# Revit family: PRD_AR_TltRllHldrs_JumboRollHolder_CHRX669,CHRX670
name_source: partatom
category: Specialty Equipment
revit_build: Autodesk Revit 2018 (Build: 20190510_1515(x64)
units: mm (PartAtom-declared; Revit-internal decimal feet)

## family parameters
Cut with Voids When Loaded = No
Host = Face
OmniClass Number = 23.40.20.21.21
OmniClass Title = Toilet Paper Dispensers
Part Type = Normal
Room Calculation Point = No
Round Connector Dimension = Use Diameter
Shared = No

## types (2) — shared parameters
AssetType = Fixed
Category = Pr_40_20_76_88, Toilet roll holders
Color = Stainless steel
Default Elevation = 700 mm  [stored 2.29659 ft]
DurationUnit = year
FillingQuantity = 1 ROLL
Finish = Satin finished
FinishAndColour = Stainless steel, satin finished
Form = Wall mounted
IfcExportAs = IfcFurnitureType
IfcExportType = NOTDEFINED
IntegralAccessories = Stainless steel screws and dowels incl.
MainColor = Stainless steel
Manufacturer = KWC Group AG
ManufacturerName = KWC Group AG
ManufacturerURL = www.kwc.com
Material = Stainless steel
Materials = Stainless steel
NBSDescription = Toilet roll holders
NBSReference = 45-35-72/368
ProductInformation = https://pim.kwc.com
RollHolderMaterial = PRD_AR_StainlessSteel_SatinFinished
Style = Toilet roll holder
URL = www.kwc.com
Uniclass2015Code = Pr_40_20_76_88
Uniclass2015Title = Toilet roll holders
Uniclass2015Version = Products v1.5
Version = 1
WarrantyDurationUnit = year

## per-type parameters (varying)
| type | BIMObjectName | Description | Features | GrossWeight | Lock | MaximumWidthOfConsumable | ModelNumber | Name | NetWeight | NominalDepth | NominalHeight | NominalLength | NominalWidth | Size |
| CHRX670 | PRD_AR_ToiletRollHolders_JumboRollHolder_CHRX670 | Jumbo roll holder for wall mounting, stainless steel, surface satin finished, material thickness 0.9 mm, closed round casing with inspection window, paper withdrawal over two tear-off edges, locked with hexagonal allen screw, for 1 roll with max. 350 mm diameter, incl. stainless steel screws, dowels and hexagonal allen key. | stainless steel, 0.90 mm, satin finished, wall mounting, 369x369x108 mm (WxHxD) | 2.42 kg | screw-lock | 100 mm  [stored 0.328084 ft] | 2000057141 | Jumbo roll holder CHRX670 | 1.90 kg | 108 mm  [stored 0.354331 ft] | 369 mm | 369 mm | 369 mm | 369 x 369 x 108 mm |
| CHRX669 | PRD_AR_ToiletRollHolders_JumboRollHolder_CHRX669 | Jumbo roll holder for wall mounting, stainless steel, surface satin finished, material thickness 0.8 mm, cylinder lock with KWC standard key, closed round casing with inspection window, paper withdrawal over two tear-off edges, for 1 roll with max. 260 mm diameter, incl. stainless steel screws and dowels. | stainless steel, 0.80 mm, satin finished, wall mounting, 269x269x116 mm (WxHxD) | 1.68 kg | key-lock | 105 mm  [stored 0.344488 ft] | 2000060983 | Jumbo roll holder CHRX669 | 1.28 kg | 116 mm  [stored 0.380577 ft] | 269 mm  [stored 0.882546 ft] | 269 mm  [stored 0.882546 ft] | 269 mm  [stored 0.882546 ft] | 269 x 269 x 116 mm |

note: column(s) folded — value = type name in every type: Model, ModelReference, Type

note: [stored X ft] marks values corroborated as IEEE doubles in the binary element streams (Revit-internal decimal feet)

## geometry (parser evidence)
native form markers: Sweep x3
no freeform markers — native parametric forms only
